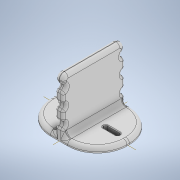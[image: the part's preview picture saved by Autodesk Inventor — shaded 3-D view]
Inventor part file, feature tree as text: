
AUTODESK INVENTOR PART (.ipt)
format: ipt  version: 2021 (Build 250183000, 183)  size: 590,336 bytes
history: native  units: mm
features: fillet x10, extrude x4, sketch x4
ambient origin geometry x8: Origin, YZ Plane, XZ Plane, XY Plane, X Axis, Y Axis, Z Axis, Center Point
bodies: Solid1 (feature_tree)
feature tree (18):
  extrude  "Extrusion1"  Depth=50.0mm
  extrude  "Extrusion2"  Depth=25.0mm
  extrude  "Extrusion3"  Depth=3.2mm
  fillet  "Fillet2"  Radius=3.2mm
  fillet  "Fillet3"  Radius=43.0mm
  fillet  "Fillet4"  Radius=11.0mm
  fillet  "Fillet5"  Radius=11.0mm
  fillet  "Fillet6"  Radius=13.0mm
  extrude  "Extrusion4"  Depth=3.5mm
  fillet  "Fillet7"  Radius=3.5mm
  fillet  "Fillet8"  Radius=1.75mm
  fillet  "Fillet9"  Radius=43.0mm
  fillet  "Fillet10"  Radius=1.5mm
  fillet  "Fillet11"  Radius=0.6mm
  sketch  "Sketch1"  dims[d0=62.0mm d1=50.0mm]
  sketch  "Sketch2"  dims[d2=31.0mm d3=25.0mm]
  sketch  "Sketch3"  dims[d4=4.0mm d5=0.0mm d6=3.2mm d7=3.2mm d8=43.0mm d9=0.0mm d11=11.0mm d12=11.0mm d13=13.0mm]
  sketch  "Sketch4"  dims[d14=13.0mm d15=3.5mm d16=3.5mm d17=1.75mm d18=43.0mm d19=0.0mm d20=1.5mm d21=0.6mm d22=24.0mm d23=4.0mm d24=3.0mm d25=5.0mm d26=5.0mm d27=5.0mm d29=12.0mm d30=13.0mm d31=13.0mm d32=5.0mm d33=5.0mm d34=5.0mm d35=13.0mm d36=13.0mm d37=5.0mm d38=0.0mm d39=3.0mm d40=2.0mm d41=2.0mm d42=2.5mm d43=4.0mm]
